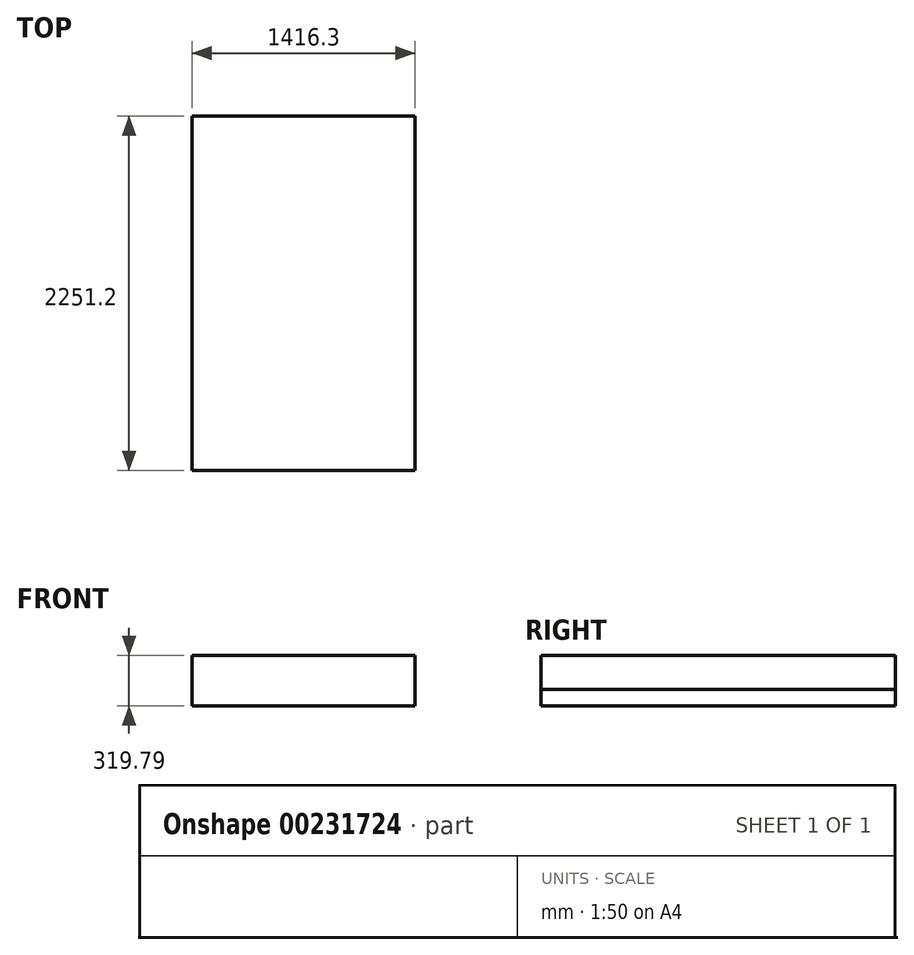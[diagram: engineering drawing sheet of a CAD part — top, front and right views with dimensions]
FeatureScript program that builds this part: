
annotation { "Feature Type Name" : "Feature", "Feature Type Description" : "" }
export const myFeature = defineFeature(function(context is Context, id is Id, definition is map)
    precondition{}
    {
        {
            var Q0;
            Q0=qCreatedBy(makeId("Top.planeOp"),FACE);
            var sketch = newSketch(context, id + "F0", { "sketchPlane" : qUnion([Q0])});
            skLineSegment(sketch, "E0.bottom", {"start": v(-1701.86, 963.2) * mm, "end": v(1703.77, 963.2) * mm});
            skLineSegment(sketch, "E0.top", {"start": v(-1701.86, -1288) * mm, "end": v(1703.77, -1288) * mm});
            skLineSegment(sketch, "E0.left", {"start": v(-1701.86, 963.2) * mm, "end": v(-1701.86, -1288) * mm});
            skLineSegment(sketch, "E0.right", {"start": v(1703.77, 963.2) * mm, "end": v(1703.77, -1288) * mm});
            skLineSegment(sketch, "E1.bottom", {"start": v(1703.77, 963.2) * mm, "end": v(709.1, 963.2) * mm});
            skLineSegment(sketch, "E1.top", {"start": v(1703.77, -1288) * mm, "end": v(709.1, -1288) * mm});
            skLineSegment(sketch, "E1.right", {"start": v(709.1, 963.2) * mm, "end": v(709.1, -1288) * mm});
            skLineSegment(sketch, "E2.bottom", {"start": v(-1701.86, 963.2) * mm, "end": v(-707.2, 963.2) * mm});
            skLineSegment(sketch, "E2.top", {"start": v(-1701.86, -1288) * mm, "end": v(-707.2, -1288) * mm});
            skLineSegment(sketch, "E2.right", {"start": v(-707.2, 963.2) * mm, "end": v(-707.2, -1288) * mm});
            skCircle(sketch, "E3", {"center": v(-1204.53, -1042.8) * mm, "radius": 128.27 * mm});
            skCircle(sketch, "E4", {"center": v(1206.44, -1042.8) * mm, "radius": 128.27 * mm});
            skCircle(sketch, "E5", {"center": v(1206.44, 716.19) * mm, "radius": 128.27 * mm});
            skCircle(sketch, "E6", {"center": v(-1204.53, 716.19) * mm, "radius": 128.27 * mm});
            skSolve(sketch);
        }
        {
            var Q0;
            Q0=makeQuery(id+"F0.imprint","IMPRINT",FACE,{"disambiguationData":[TD([[makeQuery(id+"F0.imprint","IMPRINT",EDGE,{"derivedFrom":sQuery(id+"F0.wireOp",EDGE,"E2.bottom")}),-1.0]])]});
            var Q1;
            Q1=makeQuery(id+"F0.imprint","IMPRINT",FACE,{"disambiguationData":[TD([[makeQuery(id+"F0.imprint","IMPRINT",EDGE,{"derivedFrom":sQuery(id+"F0.wireOp",EDGE,"E0.bottom")}),-1.0]])]});
            var Q2;
            Q2=makeQuery(id+"F0.imprint","IMPRINT",FACE,{"disambiguationData":[TD([[makeQuery(id+"F0.imprint","IMPRINT",EDGE,{"derivedFrom":sQuery(id+"F0.wireOp",EDGE,"E1.bottom")}),1.0]])]});
            extrude(context, id + "F1", {"entities" : qUnion([Q0, Q1, Q2]), "depth" : 416.3 * mm});
        }
        {
            var Q0;
            Q0=makeQuery(id+"F1.opExtrude","SWEPT_FACE",FACE,{"disambiguationData":[OSD([sQuery(id+"F0.wireOp",EDGE,"E0.top"),sQuery(id+"F0.wireOp",EDGE,"E1.top"),sQuery(id+"F0.wireOp",EDGE,"E2.top")])]});
            var sketch = newSketch(context, id + "F2", { "sketchPlane" : qUnion([Q0])});
            skLineSegment(sketch, "E7.bottom", {"start": v(-1701.86, 0) * mm, "end": v(-705.68, 0) * mm});
            skLineSegment(sketch, "E7.top", {"start": v(-1701.86, 103.63) * mm, "end": v(-705.68, 103.63) * mm});
            skLineSegment(sketch, "E7.left", {"start": v(-1701.86, 0) * mm, "end": v(-1701.86, 103.63) * mm});
            skLineSegment(sketch, "E7.right", {"start": v(-705.68, 0) * mm, "end": v(-705.68, 103.63) * mm});
            skLineSegment(sketch, "E8.bottom", {"start": v(1703.77, 0) * mm, "end": v(707.58, 0) * mm});
            skLineSegment(sketch, "E8.top", {"start": v(1703.77, 103.63) * mm, "end": v(707.58, 103.63) * mm});
            skLineSegment(sketch, "E8.left", {"start": v(1703.77, 0) * mm, "end": v(1703.77, 103.63) * mm});
            skLineSegment(sketch, "E8.right", {"start": v(707.58, 0) * mm, "end": v(707.58, 103.63) * mm});
            skLineSegment(sketch, "E9.bottom", {"start": v(-808.89, 416.3) * mm, "end": v(756.26, 416.3) * mm});
            skLineSegment(sketch, "E9.top", {"start": v(-808.89, 319.79) * mm, "end": v(756.26, 319.79) * mm});
            skLineSegment(sketch, "E9.left", {"start": v(-808.89, 416.3) * mm, "end": v(-808.89, 319.79) * mm});
            skLineSegment(sketch, "E9.right", {"start": v(756.26, 416.3) * mm, "end": v(756.26, 319.79) * mm});
            skSolve(sketch);
        }
        {
            var Q0;
            Q0=makeQuery(id+"F2.imprint","IMPRINT",FACE,{"disambiguationData":[TD([[makeQuery(id+"F2.imprint","IMPRINT",EDGE,{"derivedFrom":sQuery(id+"F2.wireOp",EDGE,"E9.bottom")}),-1.0]])]});
            var Q1;
            Q1=makeQuery(id+"F2.imprint","IMPRINT",FACE,{"disambiguationData":[TD([[makeQuery(id+"F2.imprint","IMPRINT",EDGE,{"derivedFrom":sQuery(id+"F2.wireOp",EDGE,"E7.bottom")}),1.0]])]});
            var Q2;
            Q2=makeQuery(id+"F2.imprint","IMPRINT",FACE,{"disambiguationData":[TD([[makeQuery(id+"F2.imprint","IMPRINT",EDGE,{"derivedFrom":sQuery(id+"F2.wireOp",EDGE,"E8.bottom")}),1.0]])]});
            extrude(context, id + "F3", {"entities" : qUnion([Q0, Q1, Q2]), "operationType" : NewBodyOperationType.REMOVE, "oppositeDirection" : true, "depth" : 2540 * mm});
        }
    });
